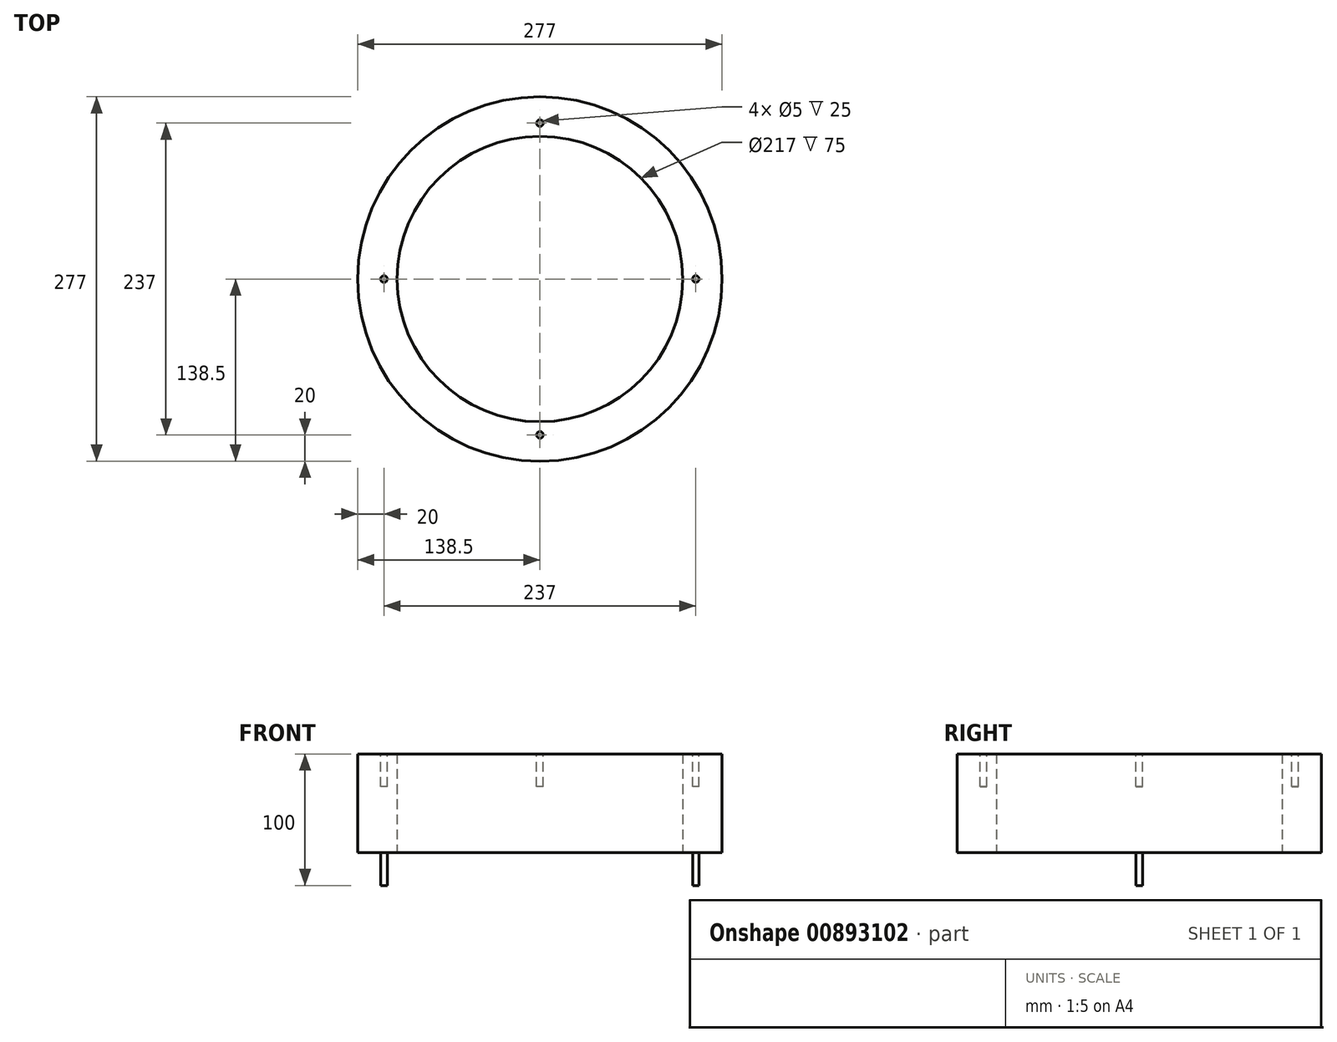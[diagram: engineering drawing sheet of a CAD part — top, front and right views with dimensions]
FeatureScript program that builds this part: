
annotation { "Feature Type Name" : "Feature", "Feature Type Description" : "" }
export const myFeature = defineFeature(function(context is Context, id is Id, definition is map)
    precondition{}
    {
        {
            var Q0;
            Q0=qCreatedBy(makeId("Top.planeOp"),FACE);
            var sketch = newSketch(context, id + "F0", { "sketchPlane" : qUnion([Q0])});
            skCircle(sketch, "E0", {"center": v(0, 0) * mm, "radius": 138.5 * mm});
            skCircle(sketch, "E1", {"center": v(0, 0) * mm, "radius": 108.5 * mm});
            skSolve(sketch);
        }
        {
            var Q0;
            Q0=makeQuery(id+"F0.imprint","IMPRINT",FACE,{"disambiguationData":[TD([[makeQuery(id+"F0.imprint","IMPRINT",EDGE,{"derivedFrom":sQuery(id+"F0.wireOp",EDGE,"E0")}),1.0]])]});
            extrude(context, id + "F1", {"entities" : qUnion([Q0]), "depth" : 100 * mm, "offsetDistance" : 25 * mm});
        }
        {
            var Q0;
            Q0=makeQuery(id+"F1.opExtrude","CAP_FACE",FACE,{"disambiguationData":[OSD([sQuery(id+"F0.wireOp",EDGE,"E0"),sQuery(id+"F0.wireOp",EDGE,"E1")])],"isStart":false});
            var sketch = newSketch(context, id + "F2", { "sketchPlane" : qUnion([Q0])});
            skCircle(sketch, "E2", {"center": v(0, 0) * mm, "radius": 118.5 * mm});
            skCircle(sketch, "E3", {"center": v(0, 118.5) * mm, "radius": 2.5 * mm});
            skCircle(sketch, "E4", {"center": v(118.5, 0) * mm, "radius": 2.5 * mm});
            skCircle(sketch, "E5", {"center": v(0, -118.5) * mm, "radius": 2.5 * mm});
            skCircle(sketch, "E6", {"center": v(-118.5, 0) * mm, "radius": 2.5 * mm});
            skSolve(sketch);
        }
        {
            var Q0;
            {var subQ0=sQuery(id+"F2.wireOp",EDGE,"E3");var subQ1=sQuery(id+"F2.wireOp",EDGE,"E2");var subQ2=makeQuery(id+"F2.imprint","INTERSECT",VERTEX,{"disambiguationData":[OD(0.0)],"derivedFrom":[subQ1,subQ0]});Q0=makeQuery(id+"F2.imprint","IMPRINT",FACE,{"disambiguationData":[TD([[makeQuery(id+"F2.imprint","IMPRINT",EDGE,{"disambiguationData":[TD([[subQ2,-1.0]])],"derivedFrom":subQ1}),-1.0]])]});}
            var Q1;
            {var subQ0=sQuery(id+"F2.wireOp",EDGE,"E3");var subQ1=sQuery(id+"F2.wireOp",EDGE,"E2");var subQ2=makeQuery(id+"F2.imprint","INTERSECT",VERTEX,{"disambiguationData":[OD(0.0)],"derivedFrom":[subQ1,subQ0]});Q1=makeQuery(id+"F2.imprint","IMPRINT",FACE,{"disambiguationData":[TD([[makeQuery(id+"F2.imprint","IMPRINT",EDGE,{"disambiguationData":[TD([[subQ2,-1.0]])],"derivedFrom":subQ1}),1.0]])]});}
            var Q2;
            {var subQ0=sQuery(id+"F2.wireOp",EDGE,"E6");var subQ1=sQuery(id+"F2.wireOp",EDGE,"E2");var subQ2=makeQuery(id+"F2.imprint","INTERSECT",VERTEX,{"disambiguationData":[OD(0.0)],"derivedFrom":[subQ1,subQ0]});Q2=makeQuery(id+"F2.imprint","IMPRINT",FACE,{"disambiguationData":[TD([[makeQuery(id+"F2.imprint","IMPRINT",EDGE,{"disambiguationData":[TD([[subQ2,-1.0]])],"derivedFrom":subQ1}),1.0]])]});}
            var Q3;
            {var subQ0=sQuery(id+"F2.wireOp",EDGE,"E6");var subQ1=sQuery(id+"F2.wireOp",EDGE,"E2");var subQ2=makeQuery(id+"F2.imprint","INTERSECT",VERTEX,{"disambiguationData":[OD(0.0)],"derivedFrom":[subQ1,subQ0]});Q3=makeQuery(id+"F2.imprint","IMPRINT",FACE,{"disambiguationData":[TD([[makeQuery(id+"F2.imprint","IMPRINT",EDGE,{"disambiguationData":[TD([[subQ2,-1.0]])],"derivedFrom":subQ1}),-1.0]])]});}
            var Q4;
            {var subQ0=sQuery(id+"F2.wireOp",EDGE,"E4");var subQ1=sQuery(id+"F2.wireOp",EDGE,"E2");var subQ2=makeQuery(id+"F2.imprint","INTERSECT",VERTEX,{"disambiguationData":[OD(0.0)],"derivedFrom":[subQ1,subQ0]});Q4=makeQuery(id+"F2.imprint","IMPRINT",FACE,{"disambiguationData":[TD([[makeQuery(id+"F2.imprint","IMPRINT",EDGE,{"disambiguationData":[TD([[subQ2,1.0]])],"derivedFrom":subQ1}),1.0]])]});}
            var Q5;
            {var subQ0=sQuery(id+"F2.wireOp",EDGE,"E4");var subQ1=sQuery(id+"F2.wireOp",EDGE,"E2");var subQ2=makeQuery(id+"F2.imprint","INTERSECT",VERTEX,{"disambiguationData":[OD(0.0)],"derivedFrom":[subQ1,subQ0]});Q5=makeQuery(id+"F2.imprint","IMPRINT",FACE,{"disambiguationData":[TD([[makeQuery(id+"F2.imprint","IMPRINT",EDGE,{"disambiguationData":[TD([[subQ2,1.0]])],"derivedFrom":subQ1}),-1.0]])]});}
            var Q6;
            {var subQ0=sQuery(id+"F2.wireOp",EDGE,"E5");var subQ1=sQuery(id+"F2.wireOp",EDGE,"E2");var subQ2=makeQuery(id+"F2.imprint","INTERSECT",VERTEX,{"disambiguationData":[OD(0.0)],"derivedFrom":[subQ1,subQ0]});Q6=makeQuery(id+"F2.imprint","IMPRINT",FACE,{"disambiguationData":[TD([[makeQuery(id+"F2.imprint","IMPRINT",EDGE,{"disambiguationData":[TD([[subQ2,-1.0]])],"derivedFrom":subQ1}),1.0]])]});}
            var Q7;
            {var subQ0=sQuery(id+"F2.wireOp",EDGE,"E5");var subQ1=sQuery(id+"F2.wireOp",EDGE,"E2");var subQ2=makeQuery(id+"F2.imprint","INTERSECT",VERTEX,{"disambiguationData":[OD(0.0)],"derivedFrom":[subQ1,subQ0]});Q7=makeQuery(id+"F2.imprint","IMPRINT",FACE,{"disambiguationData":[TD([[makeQuery(id+"F2.imprint","IMPRINT",EDGE,{"disambiguationData":[TD([[subQ2,-1.0]])],"derivedFrom":subQ1}),-1.0]])]});}
            extrude(context, id + "F3", {"entities" : qUnion([Q0, Q1, Q2, Q3, Q4, Q5, Q6, Q7]), "operationType" : NewBodyOperationType.REMOVE, "oppositeDirection" : true, "depth" : 25 * mm, "offsetDistance" : 25 * mm});
        }
        {
            var Q0;
            Q0=makeQuery(id+"F1.opExtrude","CAP_FACE",FACE,{"disambiguationData":[OSD([sQuery(id+"F0.wireOp",EDGE,"E0"),sQuery(id+"F0.wireOp",EDGE,"E1")])],"isStart":true});
            var sketch = newSketch(context, id + "F4", { "sketchPlane" : qUnion([Q0])});
            skCircle(sketch, "E7", {"center": v(0, 0) * mm, "radius": 118.5 * mm});
            skCircle(sketch, "E8", {"center": v(0, 118.5) * mm, "radius": 2.5 * mm});
            skCircle(sketch, "E9", {"center": v(118.5, 0) * mm, "radius": 2.5 * mm});
            skCircle(sketch, "E10", {"center": v(0, -118.5) * mm, "radius": 2.5 * mm});
            skCircle(sketch, "E11", {"center": v(-118.5, 0) * mm, "radius": 2.5 * mm});
            skSolve(sketch);
        }
        {
            var Q0;
            {var subQ0=sQuery(id+"F4.wireOp",EDGE,"E8");var subQ1=sQuery(id+"F4.wireOp",EDGE,"E7");var subQ2=makeQuery(id+"F4.imprint","INTERSECT",VERTEX,{"disambiguationData":[OD(0.0)],"derivedFrom":[subQ1,subQ0]});Q0=makeQuery(id+"F4.imprint","IMPRINT",FACE,{"disambiguationData":[TD([[makeQuery(id+"F4.imprint","IMPRINT",EDGE,{"disambiguationData":[TD([[subQ2,-1.0]])],"derivedFrom":subQ1}),-1.0]])]});}
            var Q1;
            {var subQ0=sQuery(id+"F4.wireOp",EDGE,"E8");var subQ1=sQuery(id+"F4.wireOp",EDGE,"E7");var subQ2=makeQuery(id+"F4.imprint","INTERSECT",VERTEX,{"disambiguationData":[OD(0.0)],"derivedFrom":[subQ1,subQ0]});Q1=makeQuery(id+"F4.imprint","IMPRINT",FACE,{"disambiguationData":[TD([[makeQuery(id+"F4.imprint","IMPRINT",EDGE,{"disambiguationData":[TD([[subQ2,-1.0]])],"derivedFrom":subQ1}),1.0]])]});}
            var Q2;
            {var subQ0=sQuery(id+"F4.wireOp",EDGE,"E11");var subQ1=sQuery(id+"F4.wireOp",EDGE,"E7");var subQ2=makeQuery(id+"F4.imprint","INTERSECT",VERTEX,{"disambiguationData":[OD(0.0)],"derivedFrom":[subQ1,subQ0]});Q2=makeQuery(id+"F4.imprint","IMPRINT",FACE,{"disambiguationData":[TD([[makeQuery(id+"F4.imprint","IMPRINT",EDGE,{"disambiguationData":[TD([[subQ2,-1.0]])],"derivedFrom":subQ1}),-1.0]])]});}
            var Q3;
            {var subQ0=sQuery(id+"F4.wireOp",EDGE,"E11");var subQ1=sQuery(id+"F4.wireOp",EDGE,"E7");var subQ2=makeQuery(id+"F4.imprint","INTERSECT",VERTEX,{"disambiguationData":[OD(0.0)],"derivedFrom":[subQ1,subQ0]});Q3=makeQuery(id+"F4.imprint","IMPRINT",FACE,{"disambiguationData":[TD([[makeQuery(id+"F4.imprint","IMPRINT",EDGE,{"disambiguationData":[TD([[subQ2,-1.0]])],"derivedFrom":subQ1}),1.0]])]});}
            var Q4;
            {var subQ0=sQuery(id+"F4.wireOp",EDGE,"E9");var subQ1=sQuery(id+"F4.wireOp",EDGE,"E7");var subQ2=makeQuery(id+"F4.imprint","INTERSECT",VERTEX,{"disambiguationData":[OD(0.0)],"derivedFrom":[subQ1,subQ0]});Q4=makeQuery(id+"F4.imprint","IMPRINT",FACE,{"disambiguationData":[TD([[makeQuery(id+"F4.imprint","IMPRINT",EDGE,{"disambiguationData":[TD([[subQ2,1.0]])],"derivedFrom":subQ1}),1.0]])]});}
            var Q5;
            {var subQ0=sQuery(id+"F4.wireOp",EDGE,"E9");var subQ1=sQuery(id+"F4.wireOp",EDGE,"E7");var subQ2=makeQuery(id+"F4.imprint","INTERSECT",VERTEX,{"disambiguationData":[OD(0.0)],"derivedFrom":[subQ1,subQ0]});Q5=makeQuery(id+"F4.imprint","IMPRINT",FACE,{"disambiguationData":[TD([[makeQuery(id+"F4.imprint","IMPRINT",EDGE,{"disambiguationData":[TD([[subQ2,1.0]])],"derivedFrom":subQ1}),-1.0]])]});}
            var Q6;
            {var subQ0=sQuery(id+"F4.wireOp",EDGE,"E10");var subQ1=sQuery(id+"F4.wireOp",EDGE,"E7");var subQ2=makeQuery(id+"F4.imprint","INTERSECT",VERTEX,{"disambiguationData":[OD(0.0)],"derivedFrom":[subQ1,subQ0]});Q6=makeQuery(id+"F4.imprint","IMPRINT",FACE,{"disambiguationData":[TD([[makeQuery(id+"F4.imprint","IMPRINT",EDGE,{"disambiguationData":[TD([[subQ2,-1.0]])],"derivedFrom":subQ1}),1.0]])]});}
            var Q7;
            {var subQ0=sQuery(id+"F4.wireOp",EDGE,"E10");var subQ1=sQuery(id+"F4.wireOp",EDGE,"E7");var subQ2=makeQuery(id+"F4.imprint","INTERSECT",VERTEX,{"disambiguationData":[OD(0.0)],"derivedFrom":[subQ1,subQ0]});Q7=makeQuery(id+"F4.imprint","IMPRINT",FACE,{"disambiguationData":[TD([[makeQuery(id+"F4.imprint","IMPRINT",EDGE,{"disambiguationData":[TD([[subQ2,-1.0]])],"derivedFrom":subQ1}),-1.0]])]});}
            extrude(context, id + "F5", {"entities" : qUnion([Q0, Q1, Q2, Q3, Q4, Q5, Q6, Q7]), "operationType" : NewBodyOperationType.REMOVE, "oppositeDirection" : true, "depth" : 25 * mm, "offsetDistance" : 25 * mm});
        }
    });
